# Revit family: EV-301 Head of Stair Local Zone Panel
name_source: partatom
category: Generic Models
revit_build: Autodesk Revit MEP 2016 (Build: 20150220_1215(x64)
units: mm (PartAtom-declared; Revit-internal decimal feet)

## family parameters
Always vertical = No
Can host rebar = No
Cut with Voids When Loaded = No
OmniClass Number = 23.40.00.00
OmniClass Title = Equipment and Furnishings
Part Type = Normal
Room Calculation Point = No
Round Connector Dimension = Use Diameter
Shared = No
Work Plane-Based = Yes

## types (1)
- Controls
    AccessibilityPerformance = Front panel removed with 6 x flat head screws
    BIMObject Category_2 = Controls
    BIMobject category = Electrical
    Colour = Light Grey
    Connection cable = 2 Core FP200 Connection
    Cost = 0 $
    Current consumption = 3A
    Default Elevation = 1000 mm  [stored 3.28084 ft]
    Depth = 85 mm  [stored 0.278871 ft]
    Description = The EV-301 interface panel monitors and control smoke
control ventilators and interface devices.
With configurable modes it can operate as a standalone
AOV control panel or as a natural shaft system or as part of
a networked mechanical solution
    Design country = UK
    Edition number = 1
    Green Tag = Easivent Text
    Height = 323 mm  [stored 1.05971 ft]
    IFC Classification = Controller
    IP rating = IP42
    Manufacturer = Easivent
    Manufacturer URL = http://easivent.co.uk
    Manufacturer country = UK
    Manufacturer name = Easivent
    Material Main = Plastic Casing - Main Box
    Model = EV-301
    NBS Reference Code = 16-16-15
    NBS Reference Description = Control Panels
    Name of the object = EV-301 Smoke Control Panel
    Nominal height = 323
    Nominal width = 301
    Notes = Please note this product may be amended without prior notification
    Plastic - Black = Black Plastic
    Product SKU = ST4 3161
    Product certification = CE 12101-10 BS ISO 21927-9
    Product data URL = http://blog.easivent.co.uk
    Product family = Control Panel
    Product group = Controls
    SerialNumber = 0
    Size = 301x323x85mm (W x D x H)
    Switch-on-duration_2 = Sensor/ Switch Controlled
    TagNumber = 0
    Technical description = The panel comes complete with two 24v reverse polarity outputs with a shared output of 3.0A, inputs for daily ventilation switches, wind/rain sensors, smoke detection and fire alarm/BMS. 
The innovative design provides a programmable facility (via DIP switches) for limited ventilation (used on day-to-day ventilation to prevent AOV windows opening fully) and timed openings which is used in conjunction with a thermostat for corridor cooling.
    To be ordered separately = All switches and controls
    Type Comments = 24V Smoke Ventilation 3A Compact Modular Control Panel
    Uniclass 2.0 Code = Pr_16_16_15
    Uniclass 2.0 Description = Control Panels
    Voltage = 24V
    WarrantyDuration = 12
    WarrantyStartDate = From items dispatch
    Weight Net (Kg) = 4.4
    Width = 301

note: [stored X ft] marks values corroborated as IEEE doubles in the binary element streams (Revit-internal decimal feet)

## geometry (parser evidence)
native form markers: Blend x4, Sweep x8
no freeform markers — native parametric forms only
